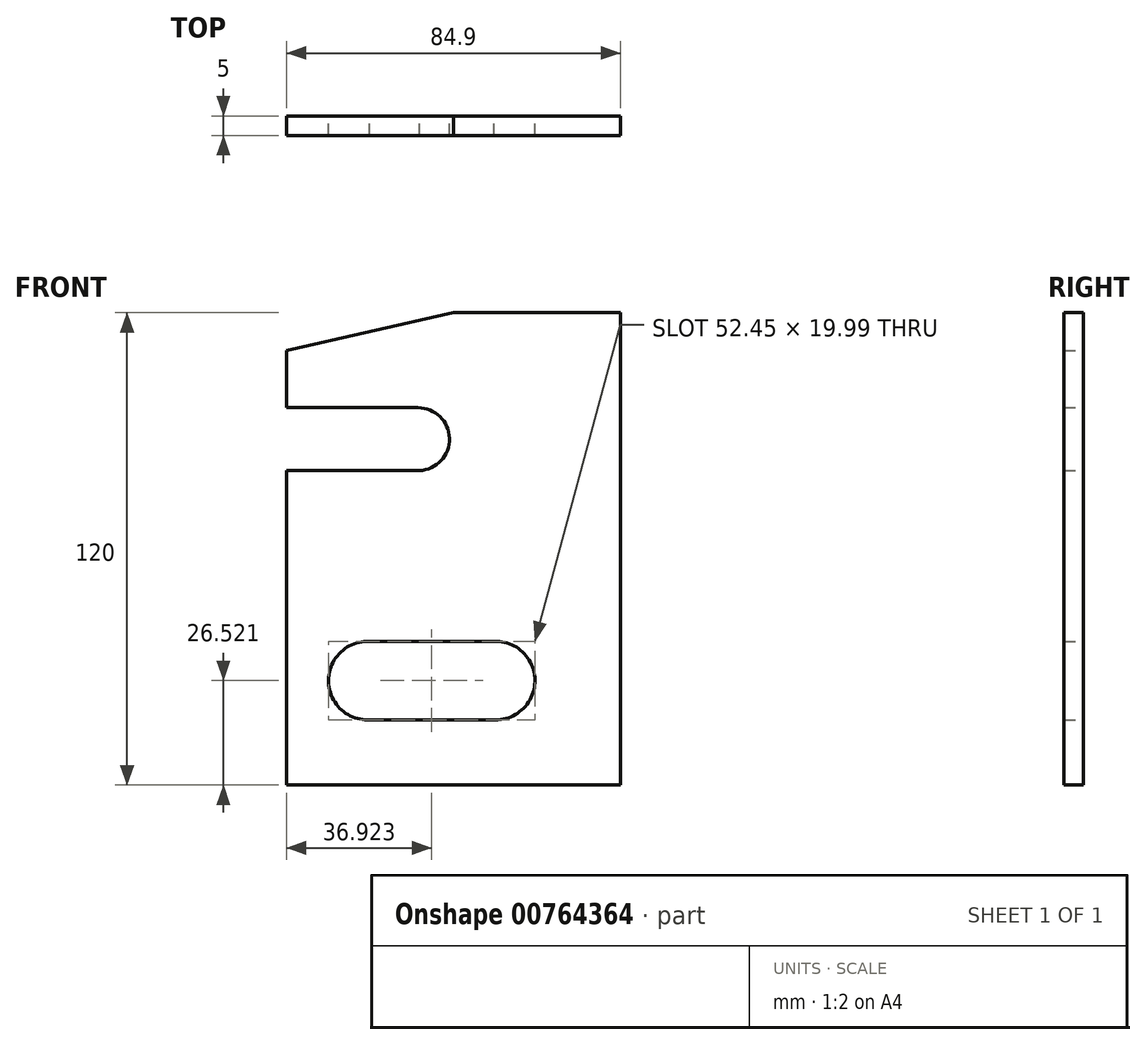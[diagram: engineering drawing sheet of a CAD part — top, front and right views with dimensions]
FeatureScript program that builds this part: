
annotation { "Feature Type Name" : "Feature", "Feature Type Description" : "" }
export const myFeature = defineFeature(function(context is Context, id is Id, definition is map)
    precondition{}
    {
        {
            var Q0;
            Q0=qCreatedBy(makeId("Front.planeOp"),FACE);
            var sketch = newSketch(context, id + "F0", { "sketchPlane" : qUnion([Q0])});
            skLineSegment(sketch, "E0.bottom", {"start": v(-0.28, 58.71) * mm, "end": v(42.17, 58.71) * mm});
            skLineSegment(sketch, "E0.top", {"start": v(-42.73, -61.29) * mm, "end": v(42.17, -61.29) * mm});
            skLineSegment(sketch, "E0.left", {"start": v(-42.73, 49.09) * mm, "end": v(-42.73, 34.58) * mm});
            skLineSegment(sketch, "E0.right", {"start": v(42.17, 58.71) * mm, "end": v(42.17, -61.29) * mm});
            skArc(sketch, "E1", {"start": v(-9.7, 18.59) * mm, "mid": v(-1.3, 26.38) * mm, "end": v(-9.3, 34.58) * mm});
            skLineSegment(sketch, "E2", {"start": v(-9.3, 34.58) * mm, "end": v(-42.73, 34.58) * mm});
            skLineSegment(sketch, "E3", {"start": v(-8.9, 18.59) * mm, "end": v(-42.73, 18.59) * mm});
            skArc(sketch, "E4", {"start": v(-21.65, -24.77) * mm, "mid": v(-32.03, -34.57) * mm, "end": v(-22.04, -44.76) * mm});
            skLineSegment(sketch, "E5.trimOffspring", {"start": v(-42.73, 18.59) * mm, "end": v(-42.73, -61.29) * mm});
            skLineSegment(sketch, "E6", {"start": v(-42.73, 49.09) * mm, "end": v(-0.28, 58.71) * mm});
            skPoint(sketch, "E7.orphan", {"position": v(-42.73, 58.71) * mm});
            skArc(sketch, "E8", {"start": v(10.42, -44.76) * mm, "mid": v(20.42, -34.57) * mm, "end": v(10.03, -24.77) * mm});
            skLineSegment(sketch, "E9", {"start": v(-22.43, -24.77) * mm, "end": v(10.81, -24.77) * mm});
            skLineSegment(sketch, "E10", {"start": v(-22.04, -44.76) * mm, "end": v(10.42, -44.76) * mm});
            skSolve(sketch);
        }
        {
            var Q0;
            Q0 = qSketchRegion(id + "F0", true);
            extrude(context, id + "F1", {"entities" : qUnion([Q0]), "depth" : 5 * mm, "offsetDistance" : 25 * mm});
        }
    });
